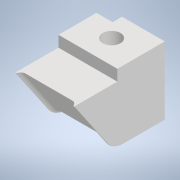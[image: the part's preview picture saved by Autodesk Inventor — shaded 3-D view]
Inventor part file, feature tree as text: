
AUTODESK INVENTOR PART (.ipt)
format: ipt  version: 2022 (Build 260153000, 153)  size: 244,736 bytes
history: native  units: mm
features: reference x10, other x9, extrude x5, sketch x5, projected_geometry x3, fillet x2, mirror x1
ambient origin geometry x8: Origin, YZ Plane, XZ Plane, XY Plane, X Axis, Y Axis, Z Axis, Center Point
bodies: Body1 (feature_tree)
feature tree (35):
  other  "Твердое тело1"
  extrude  "Выдавливание1"  Depth=0.15mm
  other  "РабПлоскость1"
  extrude  "Выдавливание4"  Depth=1.9mm
  extrude  "Выдавливание5"  Depth=9.0mm
  sketch  "Эскиз6"
  other  "РабПлоскость2"
  extrude  "Выдавливание6"  Depth=6.0mm
  extrude  "Выдавливание7"  Depth=10.6mm TaperAngle=0.0deg
  fillet  "Сопряжение4"  Radius=4.2mm
  fillet  "Сопряжение5"  Radius=3.0mm
  mirror  "Зеркальное отражение1"
  sketch  "Эскиз1"
  reference  "Ссылка1"
  reference  "Ссылка2"
  reference  "Ссылка3"
  reference  "Ссылка4"
  reference  "Ссылка5"
  reference  "Ссылка6"
  reference  "Ссылка7"
  reference  "Ссылка10"
  sketch  "Эскиз4"
  projected_geometry  "Спроецированная петля3"
  sketch  "Эскиз5"
  projected_geometry  "Спроецированная петля4"
  reference  "Ссылка11"
  reference  "Ссылка12"
  sketch  "Эскиз7"
  projected_geometry  "Спроецированная петля5"
  other  "<userpath>\Documents\Git\MZCAT_2024\MZCAT_4.iam"
  other  "MZCAT_4.iam"
  other  "base:1"
  other  "CAT_protector:1"
  other  "vydacha_slide:1"
  other  "commutationCATboard:1"
